# Revit family: Innovo GB_IR 32 285 GB LP
name_source: partatom
category: Mechanical Equipment
revit_build: Autodesk Revit 2015 (Build: 20160512_0715(x64)
units: mm (PartAtom-declared; Revit-internal decimal feet)

## types (1)
- IR-32-285 GB LP
    1e Maintenance (check-up) = 3 months after installation
    2nd Maintenance (general maintenance) = 12 months after installation
    APS Pressure < = 210.0 Pa
    Annual electricity consumption (1) = 48 kWh
    Annual electricity consumption (2) = -
    Annual fuel consumption (1) = 21 GJ GCV
    Annual fuel consumption (2) = -
    Assembly Code = D3010
    BIM Content Developer = CAD & Company
    CE-PIN = 0063CQ3037
    Co2 Emissions (tol. +/- 1.0) vol% = 10
    Cold Water Connection R = 3/4"
    Condens Discharge Connection = 40 mm  [stored 0.131234 ft]
    Default Setpoint = 65 °C
    Description = Condensing High Efficiency Storage Water Heater
    Destination / Country = UK & Ireland
    Diameter = 610 mm  [stored 2.00131 ft]
    Drain Valve Connection Rp = 3/4"
    Draw-off Capacity @ ΔT = 28°C after 120 min. = 2500.0 L
    Draw-off Capacity @ ΔT = 28°C after 30 min. = 1100.0 L
    Draw-off Capacity @ ΔT = 28°C after 60 min. = 1600.0 L
    Draw-off Capacity @ ΔT = 28°C after 90 min. = 2100.0 L
    Draw-off Capacity @ ΔT = 44°C after 120 min. = 1600.0 L
    Draw-off Capacity @ ΔT = 44°C after 30 min. = 660.0 L
    Draw-off Capacity @ ΔT = 44°C after 60 min. = 960.0 L
    Draw-off Capacity @ ΔT = 44°C after 90 min. = 1300.0 L
    Draw-off Capacity @ ΔT = 50°C after 120 min. = 1400.0 L
    Draw-off Capacity @ ΔT = 50°C after 30 min. = 570.0 L
    Draw-off Capacity @ ΔT = 50°C after 60 min. = 840.0 L
    Draw-off Capacity @ ΔT = 50°C after 90 min. = 1200.0 L
    Draw-off Capacity @ ΔT = 55°C after 120 min. = 1300.0 L
    Draw-off Capacity @ ΔT = 55°C after 30 min. = 520.0 L
    Draw-off Capacity @ ΔT = 55°C after 60 min. = 760.0 L
    Draw-off Capacity @ ΔT = 55°C after 90 min. = 1000.0 L
    Draw-off Capacity @ ΔT = 70°C after 120 min. = 960.0 L
    Draw-off Capacity @ ΔT = 70°C after 30 min. = 390.0 L
    Draw-off Capacity @ ΔT = 70°C after 60 min. = 580.0 L
    Draw-off Capacity @ ΔT = 70°C after 90 min. = 770.0 L
    Empty Weight = 136 kg
    Energy Efficiency Rating (Hi, acc NEN-EN 89-1999) = 107
    Energy Efficiency Rating (Hs, acc NEN-EN 89-1999) = 96
    Flue Diameter - concentric system = 80/125 mm/mm
    Flue Diameter - parallel system = 2x80
    Flue Diameter - water heater = 80/125 mm/mm
    Frequency = 50 Hz
    Gas Category = II2E3P
    Gas Connection R = 15"
    Gas Flow Rate - Mass kg/h = 2.3
    Gas Flow Rate - Volume ltr/hr = n.a.
    Gas Supply Pressure = 3700.0 Pa
    Heating Up Time @ ΔT = 28°C = 16
    Heating Up Time @ ΔT = 44°C = 24
    Heating Up Time @ ΔT = 50°C = 27
    Heating Up Time @ ΔT = 55°C = 30
    Heating Up Time @ ΔT = 70°C = 38
    Height = 1745 mm
    Height Air Inlet = 1350 mm
    Height Cold Water Inlet = 170 mm  [stored 0.557743 ft]
    Height Flue Outlet = 1350 mm
    Height Gas Connection = 905 mm
    Height Warm Water Outlet = 1745 mm
    Hot / Warm Water Connection R = 1"
    Indoor sound power level = 58 dB
    Installation Type = B23/C13/C33/C43/C53/C63
    Insulation Thickness = 44 mm  [stored 0.144357 ft]
    Length = 780 mm  [stored 2.55906 ft]
    Load profile = XXL
    Maintenance Interval = 12 months
    Manufacturer = A.O. Smith Water Products Company b.v.
    Manufacturer Number = E 7110
    Max. Flue Gas Outlet Temperature = 65 °C
    Max. Operating Pressure = 800000.0 Pa
    Max. Setpoint = 85 °C
    Min. Setpoint = 40 °C
    Model = IR-32-285 GB LP
    Model identifier = IR-32-285
    NOx Emissions (air free, 0% O2) ppm = 63.0/23.0
    NOx Emissions mg/kWh = 103.0/37.0
    Noice-level dB (A) = <45
    Nominal Heat Input (Gross) = 31500
    Nominal Heat Input (Net) = 29000
    Nominal Output = 30400
    Operating Weight = 438 kg
    Other load profile = -
    Packaging Height = 1895 mm
    Packaging Length = 946 mm
    Packaging Width = 786 mm
    Phase = 1
    Power Consumption (nominal) = 85 W
    Power Consumption (peak) = 105 W
    Precaustions during assembling, installation or maintenance = see User, Installation, Service and Maintenance Manual
    Recovery Rate @ ΔT = 28°C = 960.0 L/s
    Recovery Rate @ ΔT = 44°C = 610.0 L/s
    Recovery Rate @ ΔT = 50°C = 540.0 L/s
    Recovery Rate @ ΔT = 55°C = 490.0 L/s
    Recovery Rate @ ΔT = 70°C = 380.0 L/s
    Seasonal Energy Efficiency Rating = 96
    Serial Number = 8717449286361
    Smart control = No
    Stand-by Loss = 0 W
    Stand-by Loss - daily (24h) = 0 W
    Standard Set For = G31
    Storage Capacity = 285.0 L
    T&P Connection Rp = 1"
    Thermostat temperature setting = 65 °C
    Trade mark = A.O. Smith
    Transport Weight = 153 kg
    Type of Packaging = Carton and Wood
    URL = www.aosmith.co.uk
    Valve Height 01 = 693 mm  [stored 2.27362 ft]
    Valve Height 02 = 1534 mm  [stored 5.03281 ft]
    Voltage = 230 V
    Warranty on parts = 12 months
    Warranty on tank = 36 months
    Water heating energy efficiency (1) = 90%
    Water heating energy efficiency (2) = -
    Water heating energy efficiency class (1) = A
    Water heating energy efficiency class (2) = -
    Width = 610 mm  [stored 2.00131 ft]
    Working only during off-peak hour = No
    Workspace Front Distance = 1000 mm  [stored 3.28084 ft]
    Workspace Height = 2745 mm
    Workspace Radius = 780 mm  [stored 2.55906 ft]

note: [stored X ft] marks values corroborated as IEEE doubles in the binary element streams (Revit-internal decimal feet)

## geometry (parser evidence)
native form markers: Blend x26, Sweep x26
no freeform markers — native parametric forms only
